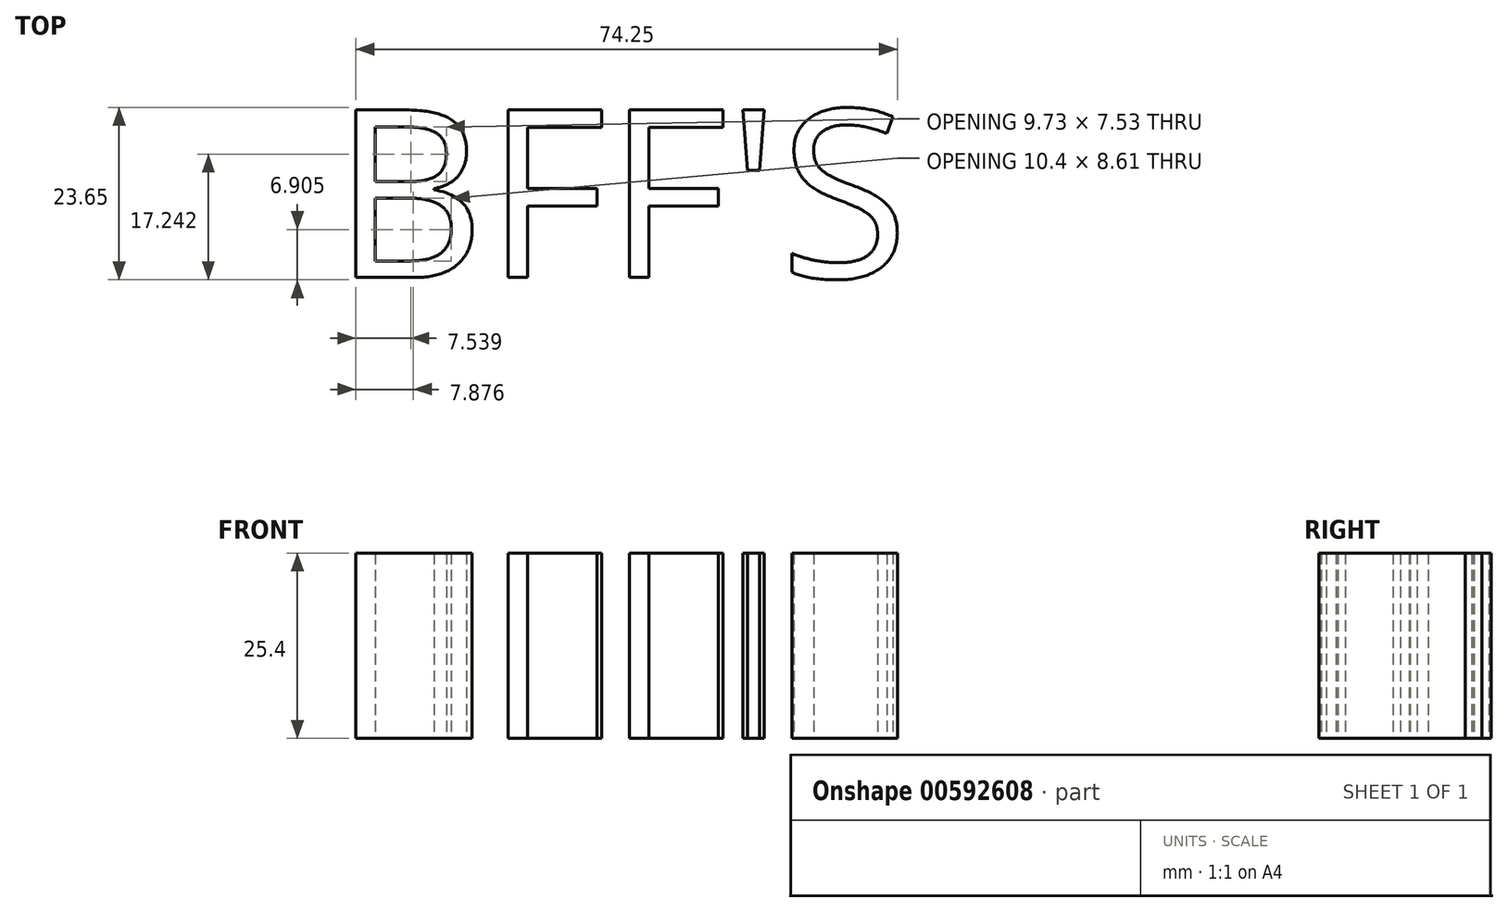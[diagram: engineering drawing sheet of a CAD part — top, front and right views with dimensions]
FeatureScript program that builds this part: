
annotation { "Feature Type Name" : "Feature", "Feature Type Description" : "" }
export const myFeature = defineFeature(function(context is Context, id is Id, definition is map)
    precondition{}
    {
        {
            var Q0;
            Q0=qCreatedBy(makeId("Top.planeOp"),FACE);
            var sketch = newSketch(context, id + "F0", { "sketchPlane" : qUnion([Q0])});
            skText(sketch, "E0", { "text": "BFF\'S", "fontName": "OpenSans-Regular.ttf"});
            const initialGuessF0  = {"E0": [-0.0426, -0.00992, 1, 0, 0.0232]};
            skSetInitialGuess(sketch, initialGuessF0);
            skSolve(sketch);
        }
        {
            var Q0;
            Q0 = qSketchRegion(id + "F0", true);
            extrude(context, id + "F1", {"entities" : qUnion([Q0]), "depth" : 25.4 * mm, "offsetDistance" : 25.4 * mm});
        }
    });
